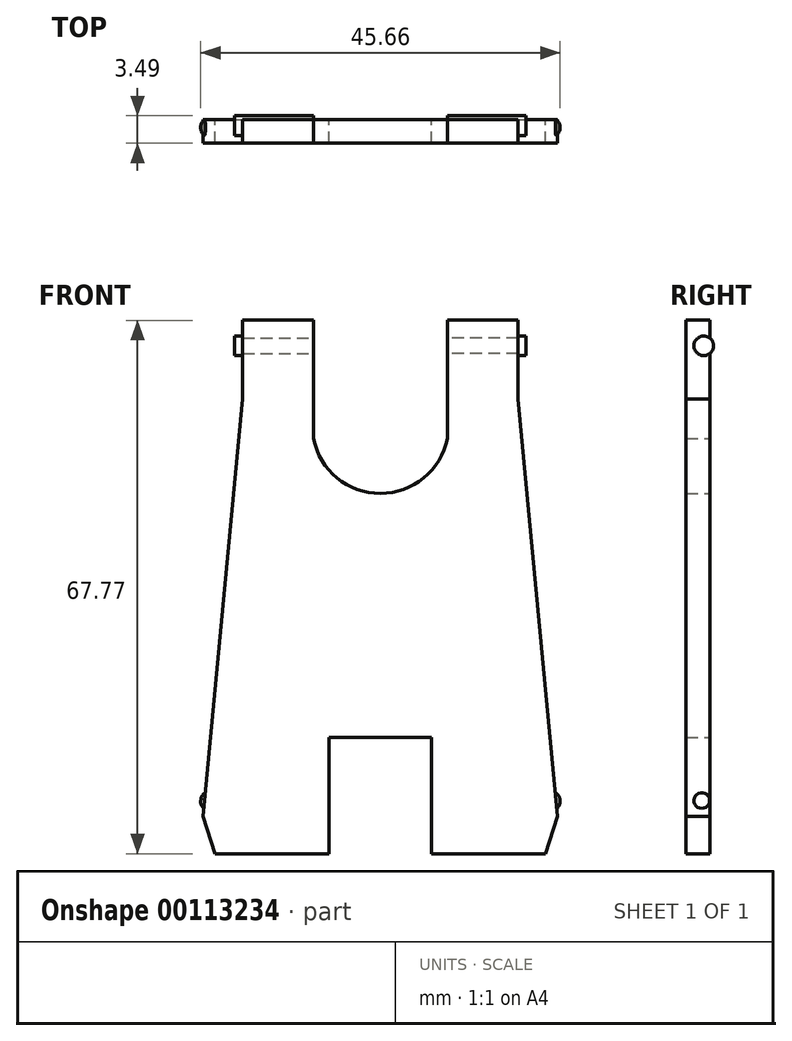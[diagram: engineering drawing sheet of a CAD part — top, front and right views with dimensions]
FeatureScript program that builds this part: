
annotation { "Feature Type Name" : "Feature", "Feature Type Description" : "" }
export const myFeature = defineFeature(function(context is Context, id is Id, definition is map)
    precondition{}
    {
        {
            var Q0;
            Q0=qCreatedBy(makeId("Front.planeOp"),FACE);
            var sketch = newSketch(context, id + "F0", { "sketchPlane" : qUnion([Q0])});
            skLineSegment(sketch, "E0", {"start": v(-13.71, 62.92) * mm, "end": v(-4.71, 62.92) * mm});
            skLineSegment(sketch, "E1", {"start": v(-4.71, 62.92) * mm, "end": v(-4.71, 52.92) * mm});
            skLineSegment(sketch, "E2", {"start": v(-4.71, 52.92) * mm, "end": v(0.29, -0.08) * mm});
            skLineSegment(sketch, "E3", {"start": v(0.29, -0.08) * mm, "end": v(-1.21, -4.85) * mm});
            skLineSegment(sketch, "E4", {"start": v(-43.21, -4.85) * mm, "end": v(-44.71, -0.08) * mm});
            skLineSegment(sketch, "E5", {"start": v(-44.71, -0.08) * mm, "end": v(-39.71, 52.92) * mm});
            skLineSegment(sketch, "E6", {"start": v(-39.71, 52.92) * mm, "end": v(-39.71, 62.92) * mm});
            skLineSegment(sketch, "E7", {"start": v(-39.71, 62.92) * mm, "end": v(-30.71, 62.92) * mm});
            skLineSegment(sketch, "E8", {"start": v(-30.71, 62.92) * mm, "end": v(-30.71, 47.92) * mm});
            skArc(sketch, "E9", {"start": v(-30.71, 47.92) * mm, "mid": v(-22.21, 40.92) * mm, "end": v(-13.71, 47.92) * mm});
            skLineSegment(sketch, "E10", {"start": v(-28.71, 9.92) * mm, "end": v(-15.71, 9.92) * mm});
            skLineSegment(sketch, "E11", {"start": v(-28.71, 9.92) * mm, "end": v(-28.71, -4.85) * mm});
            skLineSegment(sketch, "E12", {"start": v(-15.71, 9.92) * mm, "end": v(-15.71, -4.85) * mm});
            skLineSegment(sketch, "E13", {"start": v(-43.21, -4.85) * mm, "end": v(-28.71, -4.85) * mm});
            skLineSegment(sketch, "E14", {"start": v(-15.71, -4.85) * mm, "end": v(-1.21, -4.85) * mm});
            skLineSegment(sketch, "E15", {"start": v(-13.71, 47.92) * mm, "end": v(-13.71, 62.92) * mm});
            skLineSegment(sketch, "E16", {"start": v(-22.21, 49.58) * mm, "end": v(-22.21, 40.92) * mm, "construction": true});
            skLineSegment(sketch, "E17", {"start": v(-13.71, 62.92) * mm, "end": v(-30.71, 62.92) * mm, "construction": true});
            skLineSegment(sketch, "E18", {"start": v(-22.21, 49.58) * mm, "end": v(-22.21, 62.92) * mm, "construction": true});
            skSolve(sketch);
        }
        {
            var Q0;
            Q0=makeQuery(id+"F0.imprint","IMPRINT",FACE,{"disambiguationData":[TD([[makeQuery(id+"F0.imprint","IMPRINT",EDGE,{"derivedFrom":sQuery(id+"F0.wireOp",EDGE,"E0")}),-1.0]])]});
            extrude(context, id + "F1", {"entities" : qUnion([Q0]), "depth" : 3 * mm});
        }
        {
            var Q0;
            Q0=makeQuery(id+"F1.opExtrude","SWEPT_FACE",FACE,{"disambiguationData":[OSD([sQuery(id+"F0.wireOp",EDGE,"E6")])]});
            var sketch = newSketch(context, id + "F2", { "sketchPlane" : qUnion([Q0])});
            skLineSegment(sketch, "E19", {"start": v(0, 60.92) * mm, "end": v(3, 60.92) * mm, "construction": true});
            skLineSegment(sketch, "E20", {"start": v(2, 60.92) * mm, "end": v(2, 52.92) * mm, "construction": true});
            skCircle(sketch, "E21", {"center": v(0.77, 59.69) * mm, "radius": 1.25 * mm});
            skPoint(sketch, "E21.first.point", {"position": v(0.95, 60.92) * mm});
            skPoint(sketch, "E21.second.point", {"position": v(2, 59.93) * mm});
            skPoint(sketch, "E21.third.point", {"position": v(-0.44, 59.4) * mm});
            skSolve(sketch);
        }
        {
            var Q0;
            {var subQ0=sQuery(id+"F2.wireOp",EDGE,"E21");var subQ1=makeQuery(id+"F1.opExtrude","CAP_EDGE",EDGE,{"disambiguationData":[OSD([sQuery(id+"F0.wireOp",EDGE,"E6")])],"isStart":true});var subQ2=makeQuery(id+"F2.imprint","INTERSECT",VERTEX,{"disambiguationData":[OD(0.0)],"derivedFrom":[subQ1,subQ0]});Q0=makeQuery(id+"F2.imprint","IMPRINT",FACE,{"disambiguationData":[TD([[makeQuery(id+"F2.imprint","IMPRINT",EDGE,{"disambiguationData":[TD([[subQ2,1.0]])],"derivedFrom":subQ0}),1.0]])]});}
            var Q1;
            {var subQ0=sQuery(id+"F2.wireOp",EDGE,"E21");var subQ1=makeQuery(id+"F1.opExtrude","CAP_EDGE",EDGE,{"disambiguationData":[OSD([sQuery(id+"F0.wireOp",EDGE,"E6")])],"isStart":true});var subQ2=makeQuery(id+"F2.imprint","INTERSECT",VERTEX,{"disambiguationData":[OD(0.0)],"derivedFrom":[subQ1,subQ0]});Q1=makeQuery(id+"F2.imprint","IMPRINT",FACE,{"disambiguationData":[TD([[makeQuery(id+"F2.imprint","IMPRINT",EDGE,{"disambiguationData":[TD([[subQ2,-1.0]])],"derivedFrom":subQ0}),1.0]])]});}
            extrude(context, id + "F3", {"entities" : qUnion([Q0, Q1]), "operationType" : NewBodyOperationType.ADD, "depth" : 1 * mm, "hasSecondDirection" : true, "secondDirectionOppositeDirection" : true, "secondDirectionDepth" : 9 * mm});
        }
        {
            var Q0;
            Q0=makeQuery(id+"F1.opExtrude","SWEPT_FACE",FACE,{"disambiguationData":[OSD([sQuery(id+"F0.wireOp",EDGE,"E1")])]});
            var sketch = newSketch(context, id + "F4", { "sketchPlane" : qUnion([Q0])});
            skLineSegment(sketch, "E22", {"start": v(0, 60.92) * mm, "end": v(-3, 60.92) * mm, "construction": true});
            skLineSegment(sketch, "E23", {"start": v(-2, 52.92) * mm, "end": v(-2, 60.92) * mm, "construction": true});
            skCircle(sketch, "E24", {"center": v(-0.76, 59.68) * mm, "radius": 1.25 * mm});
            skPoint(sketch, "E24.first.point", {"position": v(-0.69, 60.92) * mm});
            skPoint(sketch, "E24.second.point", {"position": v(-0.5, 58.45) * mm});
            skPoint(sketch, "E24.third.point", {"position": v(-2, 59.54) * mm});
            skSolve(sketch);
        }
        {
            var Q0;
            {var subQ0=sQuery(id+"F4.wireOp",EDGE,"E24");var subQ1=makeQuery(id+"F1.opExtrude","CAP_EDGE",EDGE,{"disambiguationData":[OSD([sQuery(id+"F0.wireOp",EDGE,"E1")])],"isStart":true});var subQ2=makeQuery(id+"F4.imprint","INTERSECT",VERTEX,{"disambiguationData":[OD(0.0)],"derivedFrom":[subQ1,subQ0]});Q0=makeQuery(id+"F4.imprint","IMPRINT",FACE,{"disambiguationData":[TD([[makeQuery(id+"F4.imprint","IMPRINT",EDGE,{"disambiguationData":[TD([[subQ2,-1.0]])],"derivedFrom":subQ0}),1.0]])]});}
            var Q1;
            {var subQ0=sQuery(id+"F4.wireOp",EDGE,"E24");var subQ1=makeQuery(id+"F1.opExtrude","CAP_EDGE",EDGE,{"disambiguationData":[OSD([sQuery(id+"F0.wireOp",EDGE,"E1")])],"isStart":true});var subQ2=makeQuery(id+"F4.imprint","INTERSECT",VERTEX,{"disambiguationData":[OD(0.0)],"derivedFrom":[subQ1,subQ0]});Q1=makeQuery(id+"F4.imprint","IMPRINT",FACE,{"disambiguationData":[TD([[makeQuery(id+"F4.imprint","IMPRINT",EDGE,{"disambiguationData":[TD([[subQ2,1.0]])],"derivedFrom":subQ0}),1.0]])]});}
            extrude(context, id + "F5", {"entities" : qUnion([Q0, Q1]), "operationType" : NewBodyOperationType.ADD, "depth" : 1 * mm, "hasSecondDirection" : true, "secondDirectionOppositeDirection" : true, "secondDirectionDepth" : 9 * mm});
        }
        {
            var Q0;
            Q0=makeQuery(id+"F1.opExtrude","SWEPT_FACE",FACE,{"disambiguationData":[OSD([sQuery(id+"F0.wireOp",EDGE,"E2")])]});
            var sketch = newSketch(context, id + "F6", { "sketchPlane" : qUnion([Q0])});
            skLineSegment(sketch, "E25", {"start": v(0, 0.9) * mm, "end": v(-3, 0.9) * mm, "construction": true});
            skLineSegment(sketch, "E26", {"start": v(-2, -0.1) * mm, "end": v(-2, 0.9) * mm, "construction": true});
            skLineSegment(sketch, "E27", {"start": v(-2, 0.9) * mm, "end": v(-2, 53.13) * mm, "construction": true});
            skCircle(sketch, "E28", {"center": v(-1, 1.9) * mm, "radius": 1 * mm});
            skPoint(sketch, "E28.first.point", {"position": v(-0.93, 0.9) * mm});
            skPoint(sketch, "E28.second.point", {"position": v(-0.56, 2.79) * mm});
            skPoint(sketch, "E28.third.point", {"position": v(-2, 1.78) * mm});
            skSolve(sketch);
        }
        {
            var Q0;
            Q0=makeQuery(id+"F6.imprint","IMPRINT",FACE,{"disambiguationData":[TD([[makeQuery(id+"F6.imprint","IMPRINT",EDGE,{"derivedFrom":sQuery(id+"F6.wireOp",EDGE,"E28")}),1.0]])]});
            extrude(context, id + "F7", {"entities" : qUnion([Q0]), "operationType" : NewBodyOperationType.ADD, "depth" : .5 * mm});
        }
        {
            var Q0;
            Q0=makeQuery(id+"F1.opExtrude","SWEPT_FACE",FACE,{"disambiguationData":[OSD([sQuery(id+"F0.wireOp",EDGE,"E5")])]});
            var sketch = newSketch(context, id + "F8", { "sketchPlane" : qUnion([Q0])});
            skLineSegment(sketch, "E29", {"start": v(0, -3.27) * mm, "end": v(3, -3.27) * mm, "construction": true});
            skLineSegment(sketch, "E30", {"start": v(2, -4.27) * mm, "end": v(2, -3.27) * mm, "construction": true});
            skLineSegment(sketch, "E31", {"start": v(2, -3.27) * mm, "end": v(2, 48.96) * mm, "construction": true});
            skCircle(sketch, "E32", {"center": v(1, -2.28) * mm, "radius": 1 * mm});
            skPoint(sketch, "E32.first.point", {"position": v(0.95, -3.27) * mm});
            skPoint(sketch, "E32.second.point", {"position": v(0.74, -1.3) * mm});
            skPoint(sketch, "E32.third.point", {"position": v(2, -2.25) * mm});
            skSolve(sketch);
        }
        {
            var Q0;
            Q0=makeQuery(id+"F8.imprint","IMPRINT",FACE,{"disambiguationData":[TD([[makeQuery(id+"F8.imprint","IMPRINT",EDGE,{"derivedFrom":sQuery(id+"F8.wireOp",EDGE,"E32")}),1.0]])]});
            extrude(context, id + "F9", {"entities" : qUnion([Q0]), "operationType" : NewBodyOperationType.ADD, "depth" : .5 * mm});
        }
        {
            var Q0;
            Q0=makeQuery(id+"F7.opExtrude","CAP_EDGE",EDGE,{"disambiguationData":[OSD([sQuery(id+"F6.wireOp",EDGE,"E28")])],"isStart":false});
            var Q1;
            Q1=makeQuery(id+"F9.opExtrude","CAP_FACE",FACE,{"disambiguationData":[OSD([sQuery(id+"F8.wireOp",EDGE,"E32")])],"isStart":false});
            fillet(context, id + "F10", {"entities" : qUnion([Q0, Q1]), "radius" : 1 * mm, "tangentPropagation" : true, "allowEdgeOverflow" : false});
        }
    });
